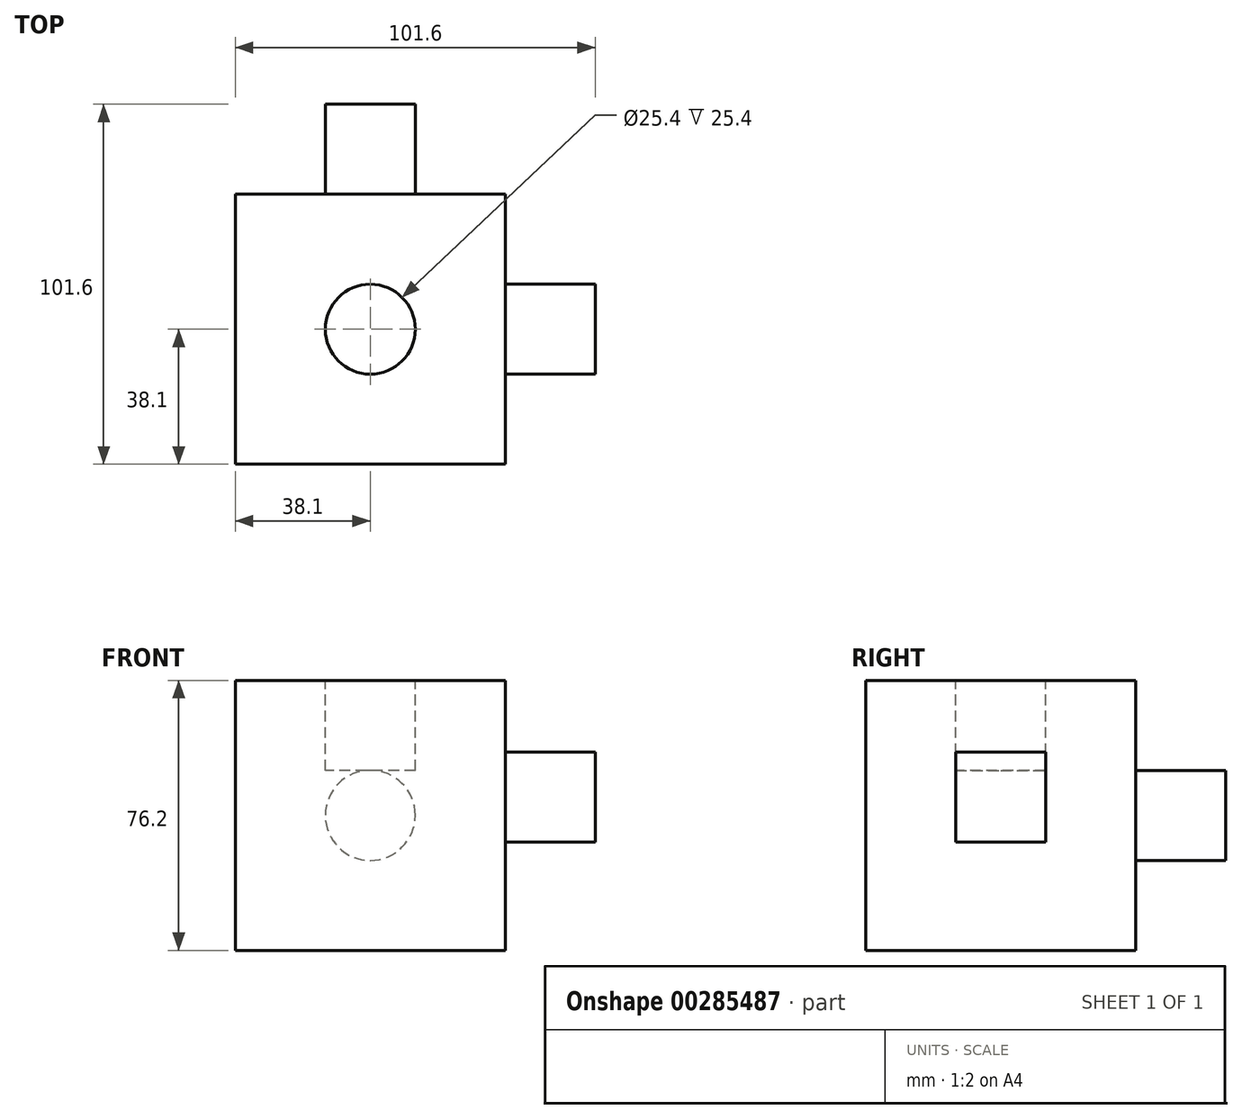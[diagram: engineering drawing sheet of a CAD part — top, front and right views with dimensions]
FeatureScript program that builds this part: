
annotation { "Feature Type Name" : "Feature", "Feature Type Description" : "" }
export const myFeature = defineFeature(function(context is Context, id is Id, definition is map)
    precondition{}
    {
        {
            var Q0;
            Q0=qCreatedBy(makeId("Front.planeOp"),FACE);
            var sketch = newSketch(context, id + "F0", { "sketchPlane" : qUnion([Q0])});
            skLineSegment(sketch, "E0.bottom", {"start": v(0, 76.2) * mm, "end": v(-76.2, 76.2) * mm});
            skLineSegment(sketch, "E0.top", {"start": v(0, 0) * mm, "end": v(-76.2, 0) * mm});
            skLineSegment(sketch, "E0.left", {"start": v(0, 76.2) * mm, "end": v(0, 0) * mm});
            skLineSegment(sketch, "E0.right", {"start": v(-76.2, 76.2) * mm, "end": v(-76.2, 0) * mm});
            skSolve(sketch);
        }
        {
            var Q0;
            Q0 = qSketchRegion(id + "F0", true);
            extrude(context, id + "F1", {"entities" : qUnion([Q0]), "depth" : 76.2 * mm});
        }
        {
            var Q0;
            Q0=makeQuery(id+"F1.opExtrude","SWEPT_FACE",FACE,{"disambiguationData":[OSD([sQuery(id+"F0.wireOp",EDGE,"E0.bottom")])]});
            var sketch = newSketch(context, id + "F2", { "sketchPlane" : qUnion([Q0])});
            skCircle(sketch, "E1", {"center": v(-38.1, -38.1) * mm, "radius": 12.7 * mm});
            skSolve(sketch);
        }
        {
            var Q0;
            Q0 = qSketchRegion(id + "F2", true);
            extrude(context, id + "F3", {"entities" : qUnion([Q0]), "operationType" : NewBodyOperationType.REMOVE, "oppositeDirection" : true, "depth" : 25.4 * mm});
        }
        {
            var Q0;
            Q0=makeQuery(id+"F1.opExtrude","SWEPT_FACE",FACE,{"disambiguationData":[OSD([sQuery(id+"F0.wireOp",EDGE,"E0.left")])]});
            var sketch = newSketch(context, id + "F4", { "sketchPlane" : qUnion([Q0])});
            skLineSegment(sketch, "E2.bottom", {"start": v(-50.8, 55.95) * mm, "end": v(-25.4, 55.95) * mm});
            skLineSegment(sketch, "E2.top", {"start": v(-50.8, 30.55) * mm, "end": v(-25.4, 30.55) * mm});
            skLineSegment(sketch, "E2.left", {"start": v(-50.8, 55.95) * mm, "end": v(-50.8, 30.55) * mm});
            skLineSegment(sketch, "E2.right", {"start": v(-25.4, 55.95) * mm, "end": v(-25.4, 30.55) * mm});
            skSolve(sketch);
        }
        {
            var Q0;
            Q0 = qSketchRegion(id + "F4", true);
            extrude(context, id + "F5", {"entities" : qUnion([Q0]), "operationType" : NewBodyOperationType.ADD, "depth" : 25.4 * mm});
        }
        {
            var Q0;
            Q0=makeQuery(id+"F1.opExtrude","CAP_FACE",FACE,{"disambiguationData":[OSD([sQuery(id+"F0.wireOp",EDGE,"E0.bottom"),sQuery(id+"F0.wireOp",EDGE,"E0.top"),sQuery(id+"F0.wireOp",EDGE,"E0.left"),sQuery(id+"F0.wireOp",EDGE,"E0.right")])],"isStart":true});
            var sketch = newSketch(context, id + "F6", { "sketchPlane" : qUnion([Q0])});
            skCircle(sketch, "E3", {"center": v(38.1, 38.1) * mm, "radius": 12.7 * mm});
            skSolve(sketch);
        }
        {
            var Q0;
            Q0 = qSketchRegion(id + "F6", true);
            extrude(context, id + "F7", {"entities" : qUnion([Q0]), "operationType" : NewBodyOperationType.ADD, "depth" : 25.4 * mm});
        }
    });
